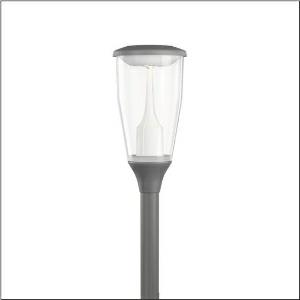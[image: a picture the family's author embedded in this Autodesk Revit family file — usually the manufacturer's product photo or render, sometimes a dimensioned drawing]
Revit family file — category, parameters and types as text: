
# Revit family: dl_11_iq___p1_0a_5xa5575nf14h000022_259a
name_source: partatom
category: Lighting Fixtures
units: mm (PartAtom-declared; Revit-internal decimal feet)

## family parameters
Cut with Voids When Loaded = No
Host = Face
Light Source = No
Part Type = Normal
Room Calculation Point = No
Round Connector Dimension = Use Diameter
Shared = No

## types (1)
- --- (1 x LED, 1530 lm, 11.8 W, 2700K)
    Apparent Load = 12 VA
    CIE Flux Codes = 34 63 91 95 100
    Color Rendering = 70
    Color Temperature = 2700K
    Default Elevation = 1800 mm
    Description = DL 11 iQ, mast luminaire, Module 540 iQ-SR, primary light control with 3 zone facetted reflector, of plastic, silver coated, highly specular, structured, primary optical cover: cover, of PMMA, transparent, light distribution: P1.0a, light emission: direct distribution, primary light characteristic: asymmetric, installation type: post-top, LED, High Power LED, rated luminous flux: 1.560lm, luminous efficacy: 149lm/W, light colour: 727, colour temperature: 2700K, control gear: iQ Street-Remote, control: Street-Remote, Auto-Match, Temp-Guard, Lumen-Switch, Night-Set, Smart-Wire, Light-Fading, Desk-Remote (wireless, voltage-free reading and setting of iQ features in the workshop via application-optimized NFC function/RFID function), optimised constant luminous flux control (CLO 2.0), mains connection: 220..240V, AC, 50/60Hz, connection cable pre-assembled, cable length: 5,5m, wiring characteristics: H07RN-F, 5-core, 1.5mm², start of lifetime: 12W, end of service life: 12W, reduction: 5W, luminaire housing, upper part, of diecast aluminium, coated, Siteco® metallic grey (DB 702S), spigot size: 76mm (post-top), mounting height: 3..5m, post-top mast mounting element, of diecast aluminium, coated, Siteco® metallic grey (DB 702S), Module 540 iQ-SR, traffic white (RAL 9016), equipment: standard, protection rating (complete): IP66, insulation class (complete): insulation class II (safety insulation), certification: CE, ENEC, ENEC+, VDE, impact resistance: IK07, packaging unit: 1 piece

Light Distribution: P1.0a
    Height = 665 mm
    Lamp = 1 x LED
    Lamp Light Flux = 1530 lm
    Lamp Power = 11.8 W
    Lamp count = 1
    Length = 334 mm
    Luminous efficacy = 130 lm/W
    Manufacturer = Siteco
    ModVariant = No
    Model = 5XA5575NF14H000022
    Number of Poles = 1
    OnlyDefault = Yes
    Power Factor = 1
    Product Name = DL 11 iQ | P1.0a
    Product group = mast luminaire | pylon top
    ProductGroupID = 6100
    Protection Class = Protection class II
    Protection Degree = IP 66
    RLX_Detail_Level = 1
    RLX_Emergency_Light_Flux = 0 lm
    RLX_Emergency_Type = 0
    RLX_Emergency_Type_DB = No
    RlxData = <blob elided: 104273 chars, md5=a9f0ff84>
    Socket = socket
    Standby Power = 0 W
    System Light Flux = 1530 lm
    System Power = 12 W
    Type Comments = factory setting: luminous flux: 100 % | dim-lin: 254 | 472 mA
    Type Image = l_1258354.jpg
    URL = http://relux.com
    VarID = @adj_113217
    Voltage = 0 V
    Weight = 0.00 kg
    Width = 0 mm  [stored 0 ft]

note: [stored X ft] marks values corroborated as IEEE doubles in the binary element streams (Revit-internal decimal feet)

## geometry (parser evidence)
native form markers: Blend x4, Sweep x10
no freeform markers — native parametric forms only
